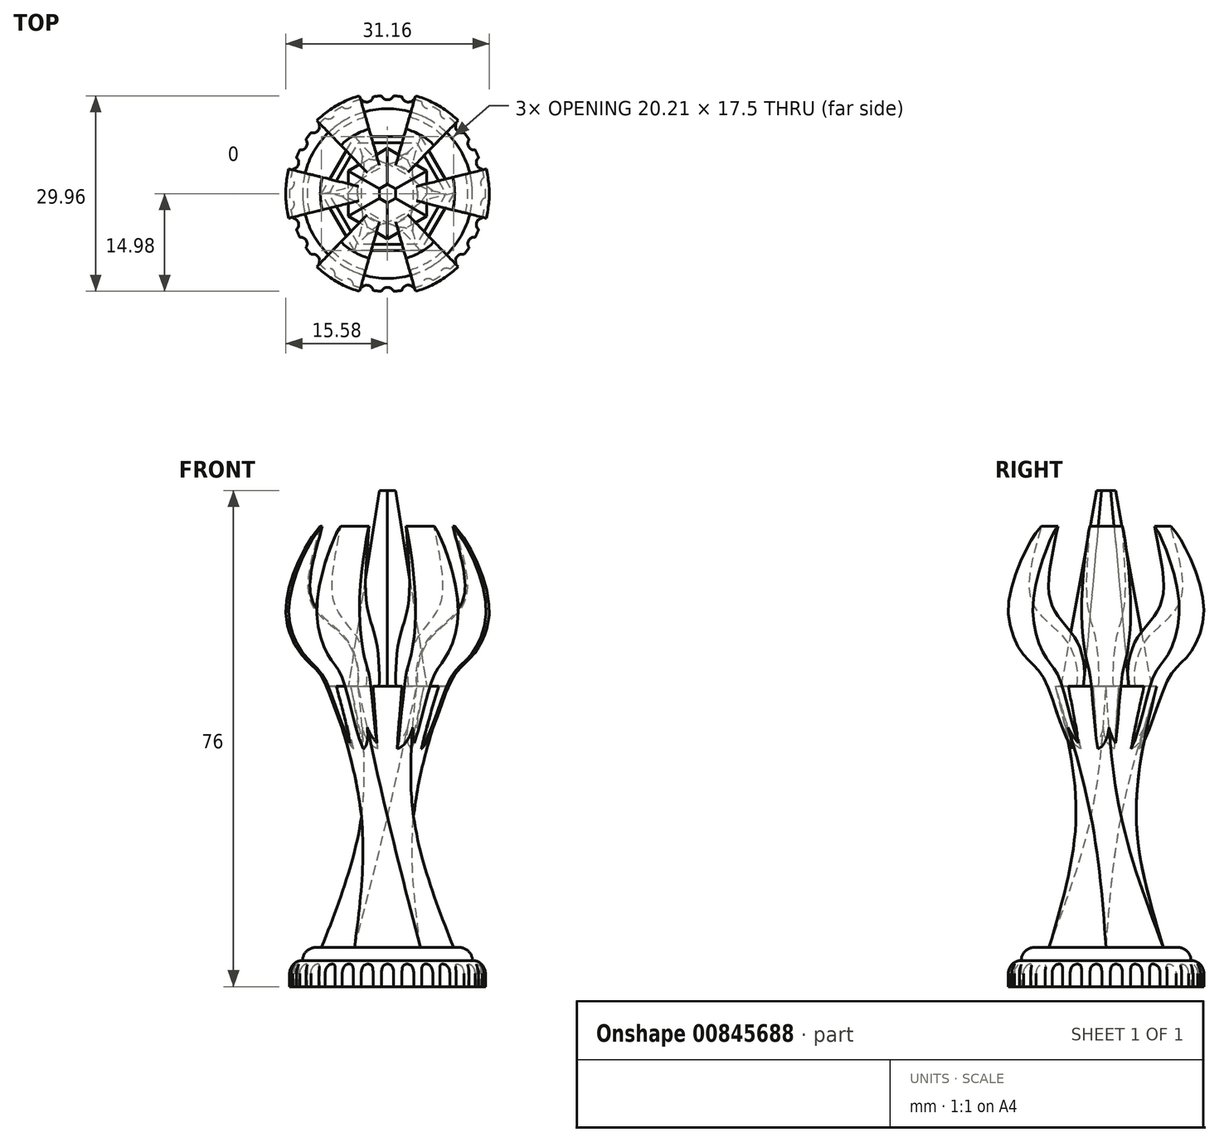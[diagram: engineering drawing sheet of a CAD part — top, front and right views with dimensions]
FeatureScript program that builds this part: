
annotation { "Feature Type Name" : "Feature", "Feature Type Description" : "" }
export const myFeature = defineFeature(function(context is Context, id is Id, definition is map)
    precondition{}
    {
        {
            var Q0;
            Q0=qCreatedBy(makeId("Top.planeOp"),FACE);
            var sketch = newSketch(context, id + "F0", { "sketchPlane" : qUnion([Q0])});
            skCircle(sketch, "E0", {"center": v(0, 0) * mm, "radius": 15 * mm});
            skSolve(sketch);
        }
        {
            var Q0;
            Q0=qSketchRegion(id+"F0",true);
            extrude(context, id + "F1", {"entities" : qUnion([Q0]), "depth" : 4 * mm, "offsetDistance" : 25 * mm});
        }
        {
            var Q0;
            Q0=makeQuery(id+"F1.opExtrude","CAP_FACE",FACE,{"disambiguationData":[OSD([sQuery(id+"F0.wireOp",EDGE,"E0")])],"isStart":false});
            var sketch = newSketch(context, id + "F2", { "sketchPlane" : qUnion([Q0])});
            skCircle(sketch, "E1", {"center": v(0, 0) * mm, "radius": 13 * mm});
            skSolve(sketch);
        }
        {
            var Q0;
            Q0=qSketchRegion(id+"F2",true);
            extrude(context, id + "F3", {"entities" : qUnion([Q0]), "operationType" : NewBodyOperationType.ADD, "depth" : 2 * mm, "offsetDistance" : 25 * mm});
        }
        {
            var Q0;
            Q0=makeQuery(id+"F1.opExtrude","CAP_EDGE",EDGE,{"disambiguationData":[OSD([sQuery(id+"F0.wireOp",EDGE,"E0")])],"isStart":false});
            var Q1;
            Q1=makeQuery(id+"F3.opExtrude","CAP_EDGE",EDGE,{"disambiguationData":[OSD([sQuery(id+"F2.wireOp",EDGE,"E1")])],"isStart":false});
            fillet(context, id + "F4", {"entities" : qUnion([Q0, Q1]), "radius" : 2 * mm, "tangentPropagation" : true, "allowEdgeOverflow" : false});
        }
        {
            var Q0;
            Q0=makeQuery(id+"F1.opExtrude","CAP_FACE",FACE,{"disambiguationData":[OSD([sQuery(id+"F0.wireOp",EDGE,"E0")])],"isStart":true});
            var sketch = newSketch(context, id + "F5", { "sketchPlane" : qUnion([Q0])});
            skCircle(sketch, "E2", {"center": v(0, 15.36) * mm, "radius": 1 * mm});
            skCircle(sketch, "E3.1.0", {"center": v(-3.2, 15.02) * mm, "radius": 1 * mm});
            skCircle(sketch, "E3.2.0", {"center": v(-6.25, 14.03) * mm, "radius": 1 * mm});
            skCircle(sketch, "E3.3.0", {"center": v(-9.03, 12.43) * mm, "radius": 1 * mm});
            skCircle(sketch, "E3.4.0", {"center": v(-11.41, 10.28) * mm, "radius": 1 * mm});
            skCircle(sketch, "E3.5.0", {"center": v(-13.3, 7.68) * mm, "radius": 1 * mm});
            skCircle(sketch, "E3.6.0", {"center": v(-14.6, 4.75) * mm, "radius": 1 * mm});
            skCircle(sketch, "E3.7.0", {"center": v(-15.27, 1.6) * mm, "radius": 1 * mm});
            skCircle(sketch, "E3.8.0", {"center": v(-15.27, -1.6) * mm, "radius": 1 * mm});
            skCircle(sketch, "E3.9.0", {"center": v(-14.6, -4.75) * mm, "radius": 1 * mm});
            skCircle(sketch, "E3.10.0", {"center": v(-13.3, -7.68) * mm, "radius": 1 * mm});
            skCircle(sketch, "E3.11.0", {"center": v(-11.41, -10.28) * mm, "radius": 1 * mm});
            skCircle(sketch, "E3.12.0", {"center": v(-9.03, -12.43) * mm, "radius": 1 * mm});
            skCircle(sketch, "E3.13.0", {"center": v(-6.25, -14.03) * mm, "radius": 1 * mm});
            skCircle(sketch, "E3.14.0", {"center": v(-3.2, -15.02) * mm, "radius": 1 * mm});
            skCircle(sketch, "E3.15.0", {"center": v(0, -15.36) * mm, "radius": 1 * mm});
            skCircle(sketch, "E3.16.0", {"center": v(3.2, -15.02) * mm, "radius": 1 * mm});
            skCircle(sketch, "E3.17.0", {"center": v(6.25, -14.03) * mm, "radius": 1 * mm});
            skCircle(sketch, "E3.18.0", {"center": v(9.03, -12.43) * mm, "radius": 1 * mm});
            skCircle(sketch, "E3.19.0", {"center": v(11.41, -10.28) * mm, "radius": 1 * mm});
            skCircle(sketch, "E3.20.0", {"center": v(13.3, -7.68) * mm, "radius": 1 * mm});
            skCircle(sketch, "E3.21.0", {"center": v(14.6, -4.75) * mm, "radius": 1 * mm});
            skCircle(sketch, "E3.22.0", {"center": v(15.27, -1.6) * mm, "radius": 1 * mm});
            skCircle(sketch, "E3.23.0", {"center": v(15.27, 1.6) * mm, "radius": 1 * mm});
            skCircle(sketch, "E3.24.0", {"center": v(14.6, 4.75) * mm, "radius": 1 * mm});
            skCircle(sketch, "E3.25.0", {"center": v(13.3, 7.68) * mm, "radius": 1 * mm});
            skCircle(sketch, "E3.26.0", {"center": v(11.41, 10.28) * mm, "radius": 1 * mm});
            skCircle(sketch, "E3.27.0", {"center": v(9.03, 12.43) * mm, "radius": 1 * mm});
            skCircle(sketch, "E3.28.0", {"center": v(6.25, 14.03) * mm, "radius": 1 * mm});
            skCircle(sketch, "E3.29.0", {"center": v(3.2, 15.02) * mm, "radius": 1 * mm});
            skPoint(sketch, "E3.center", {"position": v(0, 0) * mm});
            skSolve(sketch);
        }
        {
            var Q0;
            Q0=qSketchRegion(id+"F5",true);
            extrude(context, id + "F6", {"entities" : qUnion([Q0]), "operationType" : NewBodyOperationType.REMOVE, "oppositeDirection" : true, "depth" : 25 * mm, "offsetDistance" : 25 * mm});
        }
        {
            var Q0;
            Q0=makeQuery(id+"F3.opExtrude","CAP_FACE",FACE,{"disambiguationData":[OSD([sQuery(id+"F2.wireOp",EDGE,"E1")])],"isStart":false});
            var sketch = newSketch(context, id + "F7", { "sketchPlane" : qUnion([Q0])});
            skCircle(sketch, "E4.cCircle", {"center": v(0, 0) * mm, "radius": 8.75 * mm, "construction": true});
            skLineSegment(sketch, "E4.0", {"start": v(10.1, 0) * mm, "end": v(5.05, -8.75) * mm});
            skLineSegment(sketch, "E4.1", {"start": v(5.05, -8.75) * mm, "end": v(-5.05, -8.75) * mm});
            skLineSegment(sketch, "E4.2", {"start": v(-5.05, -8.75) * mm, "end": v(-10.1, 0) * mm});
            skLineSegment(sketch, "E4.3", {"start": v(-10.1, 0) * mm, "end": v(-5.05, 8.75) * mm});
            skLineSegment(sketch, "E4.4", {"start": v(-5.05, 8.75) * mm, "end": v(5.05, 8.75) * mm});
            skLineSegment(sketch, "E4.5", {"start": v(5.05, 8.75) * mm, "end": v(10.1, 0) * mm});
            skPoint(sketch, "E4.0.midPoint", {"position": v(7.58, -4.38) * mm});
            skSolve(sketch);
        }
        {
            var Q0;
            Q0=makeQuery(id+"F7.imprint","IMPRINT",FACE,{"disambiguationData":[TD([[makeQuery(id+"F7.imprint","IMPRINT",EDGE,{"derivedFrom":sQuery(id+"F7.wireOp",EDGE,"E4.0")}),1.0]])]});
            cPlane(context, id + "F8", {"entities" : qUnion([Q0]), "cplaneType" : CPlaneType.OFFSET, "offset" : 20 * mm, "width" : 150 * mm, "height" : 150 * mm});
        }
        {
            var Q0;
            Q0=qCreatedBy(id+"F8.planeOp",FACE);
            cPlane(context, id + "F9", {"entities" : qUnion([Q0]), "cplaneType" : CPlaneType.OFFSET, "offset" : 20 * mm, "width" : 150 * mm, "height" : 150 * mm});
        }
        {
            var Q0;
            Q0=qCreatedBy(id+"F8.planeOp",FACE);
            var sketch = newSketch(context, id + "F10", { "sketchPlane" : qUnion([Q0])});
            skCircle(sketch, "E5.cCircle", {"center": v(0, 0) * mm, "radius": 4 * mm, "construction": true});
            skLineSegment(sketch, "E5.0", {"start": v(4, 2.3) * mm, "end": v(4, -2.3) * mm});
            skLineSegment(sketch, "E5.1", {"start": v(4, -2.3) * mm, "end": v(0, -4.62) * mm});
            skLineSegment(sketch, "E5.2", {"start": v(0, -4.62) * mm, "end": v(-4, -2.3) * mm});
            skLineSegment(sketch, "E5.3", {"start": v(-4, -2.3) * mm, "end": v(-4, 2.3) * mm});
            skLineSegment(sketch, "E5.4", {"start": v(-4, 2.3) * mm, "end": v(0, 4.62) * mm});
            skLineSegment(sketch, "E5.5", {"start": v(0, 4.62) * mm, "end": v(4, 2.3) * mm});
            skPoint(sketch, "E5.0.midPoint", {"position": v(4, 0) * mm});
            skSolve(sketch);
        }
        {
            var Q0;
            Q0=qCreatedBy(id+"F9.planeOp",FACE);
            var sketch = newSketch(context, id + "F11", { "sketchPlane" : qUnion([Q0])});
            skCircle(sketch, "E6.cCircle", {"center": v(0, 0) * mm, "radius": 7.75 * mm, "construction": true});
            skLineSegment(sketch, "E6.0", {"start": v(-4.47, 7.75) * mm, "end": v(4.47, 7.75) * mm});
            skLineSegment(sketch, "E6.1", {"start": v(4.47, 7.75) * mm, "end": v(8.95, 0) * mm});
            skLineSegment(sketch, "E6.2", {"start": v(8.95, 0) * mm, "end": v(4.47, -7.75) * mm});
            skLineSegment(sketch, "E6.3", {"start": v(4.47, -7.75) * mm, "end": v(-4.47, -7.75) * mm});
            skLineSegment(sketch, "E6.4", {"start": v(-4.47, -7.75) * mm, "end": v(-8.95, 0) * mm});
            skLineSegment(sketch, "E6.5", {"start": v(-8.95, 0) * mm, "end": v(-4.47, 7.75) * mm});
            skPoint(sketch, "E6.0.midPoint", {"position": v(0, 7.75) * mm});
            skSolve(sketch);
        }
        {
            var Q1;
            Q1=makeQuery(id+"F7.imprint","IMPRINT",FACE,{"disambiguationData":[TD([[makeQuery(id+"F7.imprint","IMPRINT",EDGE,{"derivedFrom":sQuery(id+"F7.wireOp",EDGE,"E4.0")}),-1.0]])]});
            var Q2;
            Q2=makeQuery(id+"F10.imprint","IMPRINT",FACE,{"disambiguationData":[TD([[makeQuery(id+"F10.imprint","IMPRINT",EDGE,{"derivedFrom":sQuery(id+"F10.wireOp",EDGE,"E5.0")}),-1.0]])]});
            var Q3;
            Q3=makeQuery(id+"F11.imprint","IMPRINT",FACE,{"disambiguationData":[TD([[makeQuery(id+"F11.imprint","IMPRINT",EDGE,{"derivedFrom":sQuery(id+"F11.wireOp",EDGE,"E6.0")}),-1.0]])]});
            var Q4;
            Q4=sQuery(id+"F7.wireOp",VERTEX,"E4.2.end");
            var Q5;
            Q5=sQuery(id+"F10.wireOp",VERTEX,"E5.3.end");
            var Q6;
            Q6=sQuery(id+"F11.wireOp",VERTEX,"E6.0.start");
            loft(context, id + "F12", {"operationType" : NewBodyOperationType.ADD, "sheetProfilesArray" : [{ "sheetProfileEntities" : qUnion([Q1]) }, { "sheetProfileEntities" : qUnion([Q2]) }, { "sheetProfileEntities" : qUnion([Q3]) }], "matchConnections" : true, "connections" : [{ "connectionEntities" : qUnion([Q4, Q5, Q6]), "connectionEdgeQueries" : qUnion([]), "connectionEdgeParameters" : [] }]});
        }
        {
            var Q0;
            Q0=qCreatedBy(makeId("Front.planeOp"),FACE);
            var sketch = newSketch(context, id + "F13", { "sketchPlane" : qUnion([Q0])});
            skLineSegment(sketch, "E7", {"start": v(0, 0) * mm, "end": v(0, 62.44) * mm, "construction": true});
            skSolve(sketch);
        }
        {
            var Q0;
            Q0=qCreatedBy(makeId("Front.planeOp"),FACE);
            var sketch = newSketch(context, id + "F14", { "sketchPlane" : qUnion([Q0])});
            skFitSpline(sketch, "E8", {"points": [v(-5.21, 36.26) * mm, v(-9.94, 47.2) * mm, v(-12.88, 50.53) * mm, v(-15.57, 58.12) * mm, v(-11.58, 68.95) * mm, v(-10.29, 70.55) * mm], "startDerivative": vector(-22.68, 30.74) * mm, "endDerivative": vector(9.32, 10.03) * mm});
            skFitSpline(sketch, "E9", {"points": [v(-5.21, 36.26) * mm, v(-5.06, 41.11) * mm, v(-5.21, 44.6) * mm], "startDerivative": vector(6.65, 6.53) * mm, "endDerivative": vector(1.42, 12.01) * mm});
            skFitSpline(sketch, "E10", {"points": [v(-5.21, 44.6) * mm, v(-4.54, 47.04) * mm, v(-5.79, 52.25) * mm, v(-9.46, 56) * mm, v(-12.2, 60.59) * mm, v(-10.29, 70.55) * mm], "startDerivative": vector(7.83, 14.65) * mm, "endDerivative": vector(7.48, 29.36) * mm});
            skSolve(sketch);
        }
        {
            var Q0;
            Q0=qSketchRegion(id+"F14",true);
            var Q1;
            Q1=sQuery(id+"F13.wireOp",EDGE,"E7");
            revolve(context, id + "F15", {"operationType" : NewBodyOperationType.ADD, "surfaceOperationType" : NewSurfaceOperationType.NEW, "entities" : qUnion([Q0]), "axis" : qUnion([Q1]), "revolveType" : RevolveType.SYMMETRIC, "angle" : 28 * degree});
        }
        {
            var Q0;
            Q0=makeQuery(id+"F1.opExtrude","SWEPT_BODY",BODY,{"disambiguationData":[OSD([sQuery(id+"F0.wireOp",EDGE,"E0")])]});
            var Q1;
            Q1=sQuery(id+"F13.wireOp",EDGE,"E7");
            circularPattern(context, id + "F16", {"entities" : qUnion([Q0]), "axis" : qUnion([Q1]), "angle" : 360 * degree, "instanceCount" : 6, "equalSpace" : true});
        }
        {
            var Q0;
            Q0=makeQuery(id+"F11.imprint","IMPRINT",FACE,{"disambiguationData":[TD([[makeQuery(id+"F11.imprint","IMPRINT",EDGE,{"derivedFrom":sQuery(id+"F11.wireOp",EDGE,"E6.0")}),-1.0]])]});
            var sketch = newSketch(context, id + "F17", { "sketchPlane" : qUnion([Q0])});
            skCircle(sketch, "E11.cCircle", {"center": v(0, 0) * mm, "radius": 6 * mm, "construction": true});
            skLineSegment(sketch, "E11.0", {"start": v(6, 3.46) * mm, "end": v(6, -3.46) * mm});
            skLineSegment(sketch, "E11.1", {"start": v(6, -3.46) * mm, "end": v(0, -6.93) * mm});
            skLineSegment(sketch, "E11.2", {"start": v(0, -6.93) * mm, "end": v(-6, -3.46) * mm});
            skLineSegment(sketch, "E11.3", {"start": v(-6, -3.46) * mm, "end": v(-6, 3.46) * mm});
            skLineSegment(sketch, "E11.4", {"start": v(-6, 3.46) * mm, "end": v(0, 6.93) * mm});
            skLineSegment(sketch, "E11.5", {"start": v(0, 6.93) * mm, "end": v(6, 3.46) * mm});
            skPoint(sketch, "E11.0.midPoint", {"position": v(6, 0) * mm});
            skSolve(sketch);
        }
        {
            var Q0;
            Q0=makeQuery(id+"F17.imprint","IMPRINT",FACE,{"disambiguationData":[TD([[makeQuery(id+"F17.imprint","IMPRINT",EDGE,{"derivedFrom":sQuery(id+"F17.wireOp",EDGE,"E11.0")}),-1.0]])]});
            extrude(context, id + "F18", {"entities" : qUnion([Q0]), "depth" : 30 * mm, "offsetDistance" : 25 * mm, "hasDraft" : true, "draftAngle" : 9 * degree, "draftPullDirection" : true});
        }
    });
